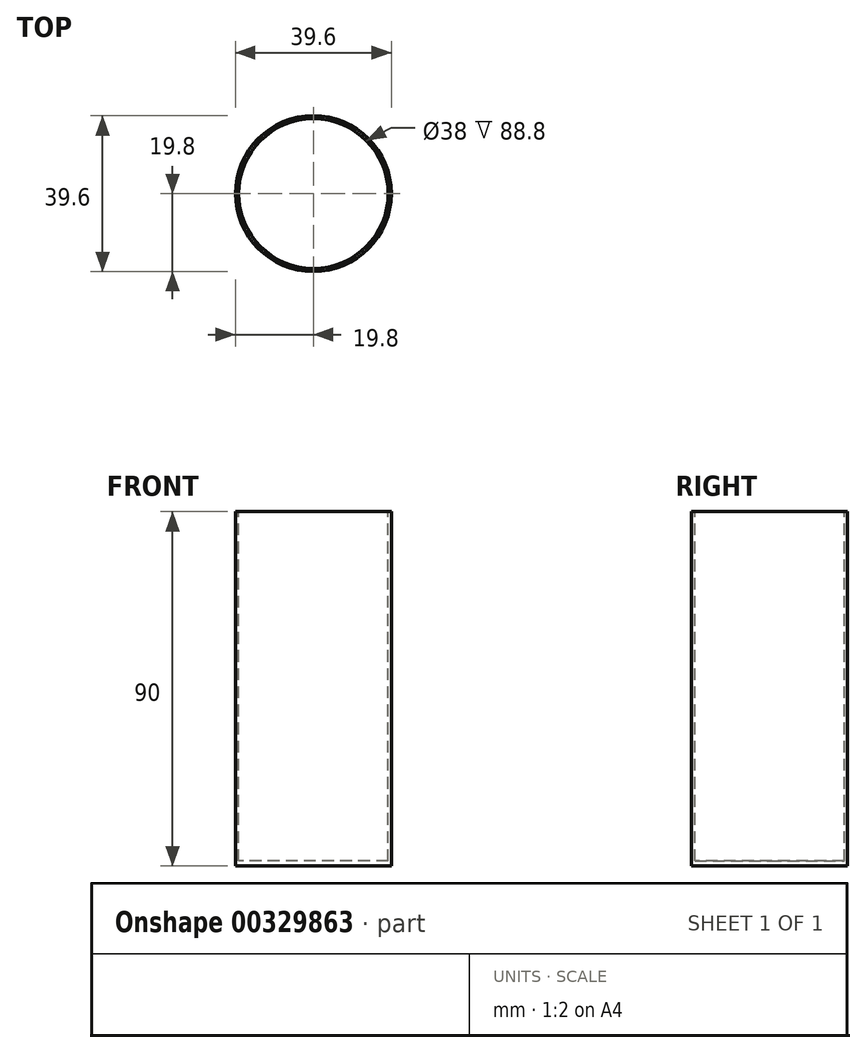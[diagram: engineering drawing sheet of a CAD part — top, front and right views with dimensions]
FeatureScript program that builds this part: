
annotation { "Feature Type Name" : "Feature", "Feature Type Description" : "" }
export const myFeature = defineFeature(function(context is Context, id is Id, definition is map)
    precondition{}
    {
        {
            var Q0;
            Q0=qCreatedBy(makeId("Front.planeOp"),FACE);
            var sketch = newSketch(context, id + "F0", { "sketchPlane" : qUnion([Q0])});
            skLineSegment(sketch, "E0", {"start": v(0, 0) * mm, "end": v(19.8, 0) * mm});
            skLineSegment(sketch, "E1", {"start": v(19.8, 0) * mm, "end": v(19.8, 90) * mm});
            skLineSegment(sketch, "E2", {"start": v(19.8, 90) * mm, "end": v(19, 90) * mm});
            skLineSegment(sketch, "E3", {"start": v(19, 90) * mm, "end": v(19, 1.2) * mm});
            skLineSegment(sketch, "E4", {"start": v(19, 1.2) * mm, "end": v(0, 1.2) * mm});
            skLineSegment(sketch, "E5", {"start": v(0, 1.2) * mm, "end": v(0, 0) * mm});
            skSolve(sketch);
        }
        {
            var Q0;
            Q0 = qSketchRegion(id + "F0", true);
            var Q1;
            Q1=sQuery(id+"F0.wireOp",EDGE,"E5");
            revolve(context, id + "F1", {"surfaceOperationType" : NewSurfaceOperationType.NEW, "entities" : qUnion([Q0]), "axis" : qUnion([Q1]), "revolveType" : RevolveType.FULL});
        }
    });
